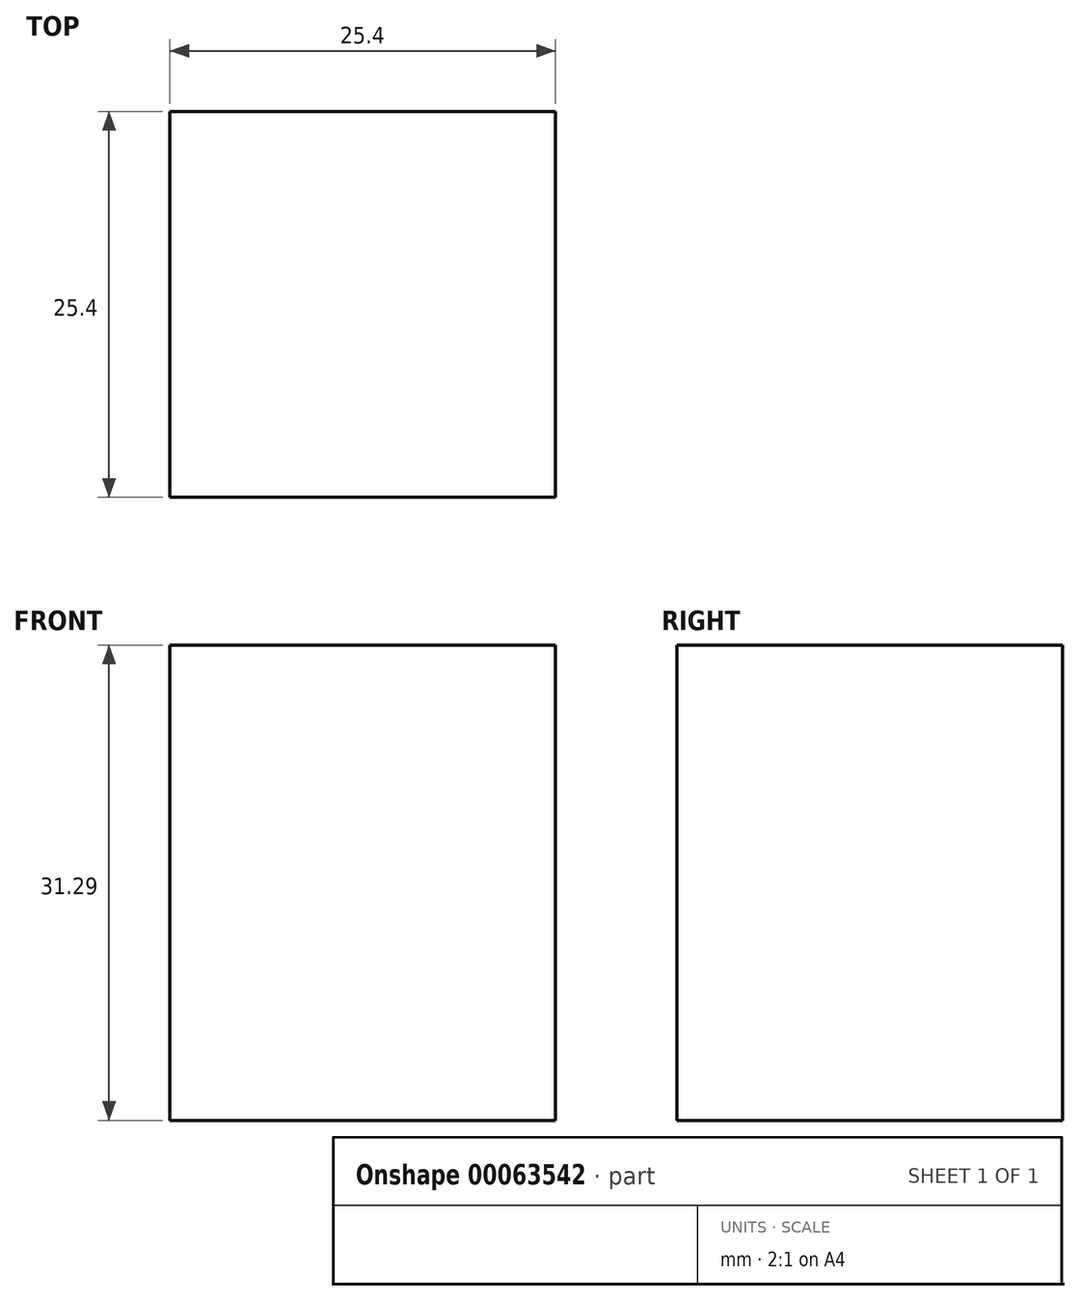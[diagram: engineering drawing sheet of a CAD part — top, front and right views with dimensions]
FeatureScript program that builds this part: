
annotation { "Feature Type Name" : "Feature", "Feature Type Description" : "" }
export const myFeature = defineFeature(function(context is Context, id is Id, definition is map)
    precondition{}
    {
        {
            var Q0;
            Q0=qCreatedBy(makeId("Top.planeOp"),FACE);
            var sketch = newSketch(context, id + "F0", { "sketchPlane" : qUnion([Q0])});
            skLineSegment(sketch, "E0.bottom", {"start": v(-44.47, -20.63) * mm, "end": v(-19.07, -20.63) * mm});
            skLineSegment(sketch, "E0.top", {"start": v(-44.47, -46.03) * mm, "end": v(-19.07, -46.03) * mm});
            skLineSegment(sketch, "E0.left", {"start": v(-44.47, -20.63) * mm, "end": v(-44.47, -46.03) * mm});
            skLineSegment(sketch, "E0.right", {"start": v(-19.07, -20.63) * mm, "end": v(-19.07, -46.03) * mm});
            skSolve(sketch);
        }
        {
            var Q0;
            Q0=makeQuery(id+"F0.imprint","IMPRINT",FACE,{"disambiguationData":[TD([[makeQuery(id+"F0.imprint","IMPRINT",EDGE,{"derivedFrom":sQuery(id+"F0.wireOp",EDGE,"E0.bottom")}),-1.0]])]});
            extrude(context, id + "F1", {"entities" : qUnion([Q0]), "depth" : 31.3 * mm});
        }
    });
